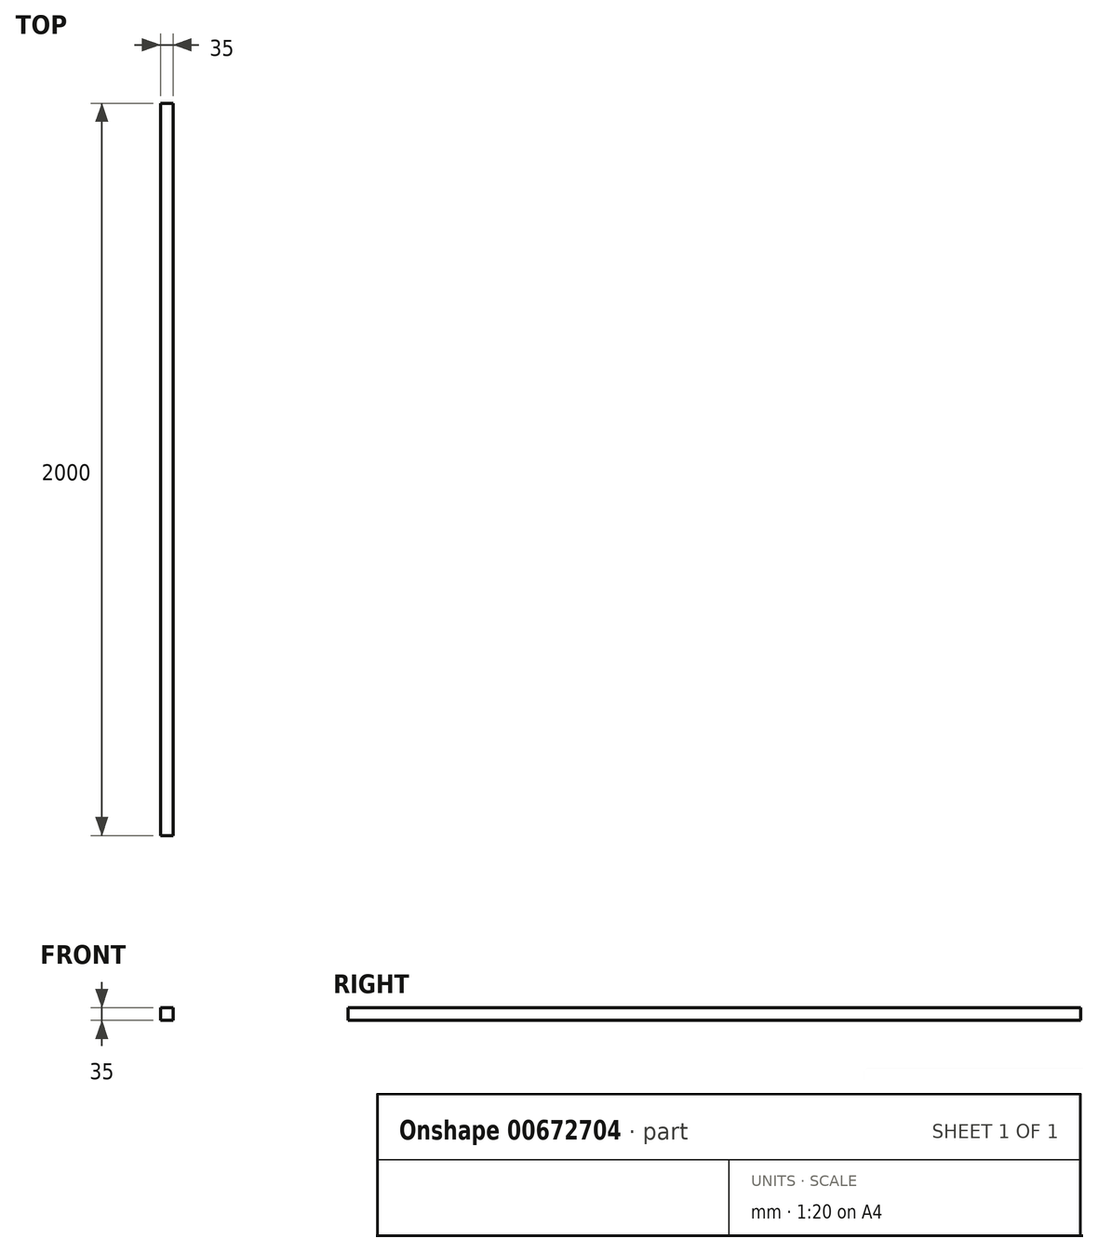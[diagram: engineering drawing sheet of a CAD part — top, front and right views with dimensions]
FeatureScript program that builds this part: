
annotation { "Feature Type Name" : "Feature", "Feature Type Description" : "" }
export const myFeature = defineFeature(function(context is Context, id is Id, definition is map)
    precondition{}
    {
        {
            var Q0;
            Q0=qCreatedBy(makeId("Front.planeOp"),FACE);
            var sketch = newSketch(context, id + "F0", { "sketchPlane" : qUnion([Q0])});
            skLineSegment(sketch, "E0.bottom", {"start": v(0, 0) * mm, "end": v(35, 0) * mm});
            skLineSegment(sketch, "E0.top", {"start": v(0, 35) * mm, "end": v(35, 35) * mm});
            skLineSegment(sketch, "E0.left", {"start": v(0, 0) * mm, "end": v(0, 35) * mm});
            skLineSegment(sketch, "E0.right", {"start": v(35, 0) * mm, "end": v(35, 35) * mm});
            skSolve(sketch);
        }
        {
            var Q0;
            Q0=makeQuery(id+"F0.imprint","IMPRINT",FACE,{"disambiguationData":[TD([[makeQuery(id+"F0.imprint","IMPRINT",EDGE,{"derivedFrom":sQuery(id+"F0.wireOp",EDGE,"E0.bottom")}),1.0]])]});
            extrude(context, id + "F1", {"entities" : qUnion([Q0]), "depth" : 2000 * mm, "offsetDistance" : 25 * mm});
        }
    });
